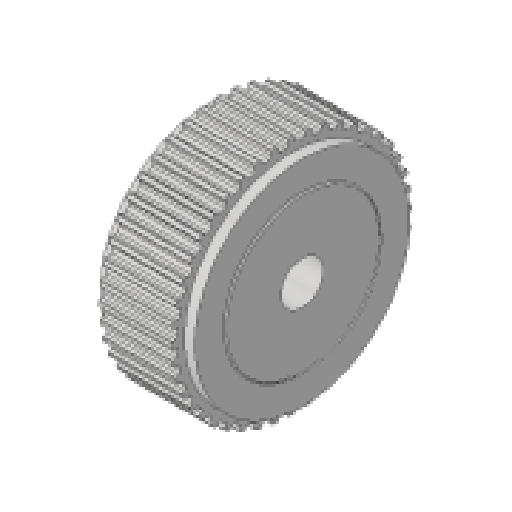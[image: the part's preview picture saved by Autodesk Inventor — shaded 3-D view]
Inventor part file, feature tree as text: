
AUTODESK INVENTOR PART (.ipt)
format: ipt  version: 2025.1 (Build 291241000, 241)  size: 677,888 bytes
history: native  units: mm
features: other x21, sketch x4, extrude x3, revolve x1
ambient origin geometry x8: Origin, YZ Plane, XZ Plane, XY Plane, X Axis, Y Axis, Z Axis, Center Point
bodies: Solid1 (feature_tree)
feature tree (29):
  revolve  "Revolution1"  [1 undecoded]
  extrude  "Extrusion1"  TaperAngle=0.0deg  [1 undecoded]
  other  "FLL_XY"
  other  "FLL_YZ"
  other  "FLL_ZX"
  other  "FLL_X"
  other  "FLL_Y"
  other  "FLL_Z"
  other  "FLL_Center"
  other  "FLR_XY"
  other  "FLR_YZ"
  other  "FLR_ZX"
  other  "FLR_X"
  other  "FLR_Y"
  other  "FLR_Z"
  other  "FLR_Center"
  other  "MXL025_D_XY"
  other  "MXL025_D_YZ"
  other  "MXL025_D_ZX"
  other  "MXL025_D_X"
  other  "MXL025_D_Y"
  other  "MXL025_D_Z"
  other  "MXL025_D_Center"
  extrude  "Wyciągnięcie proste2"  TaperAngle=0.0deg  [1 undecoded]
  extrude  "Wyciągnięcie proste3"  Depth=10.0mm TaperAngle=0.0deg
  sketch  "Sketch_5"  dims[d3=0.0mm d4=0.0mm d5=0.0mm d6=10.0mm d7=0.0mm d8=0.2mm d9=0.0mm]
  sketch  "Sketch_3"  dims[d0=360.0deg d1=11.0mm d2=0.0mm]
  sketch  "Szkic3"
  sketch  "Szkic4"
note: 3 required parameter values undecoded (feature->parameter linkage not recoverable at this tier; creation-order binding heuristic only, values carry confidence <= 0.55)